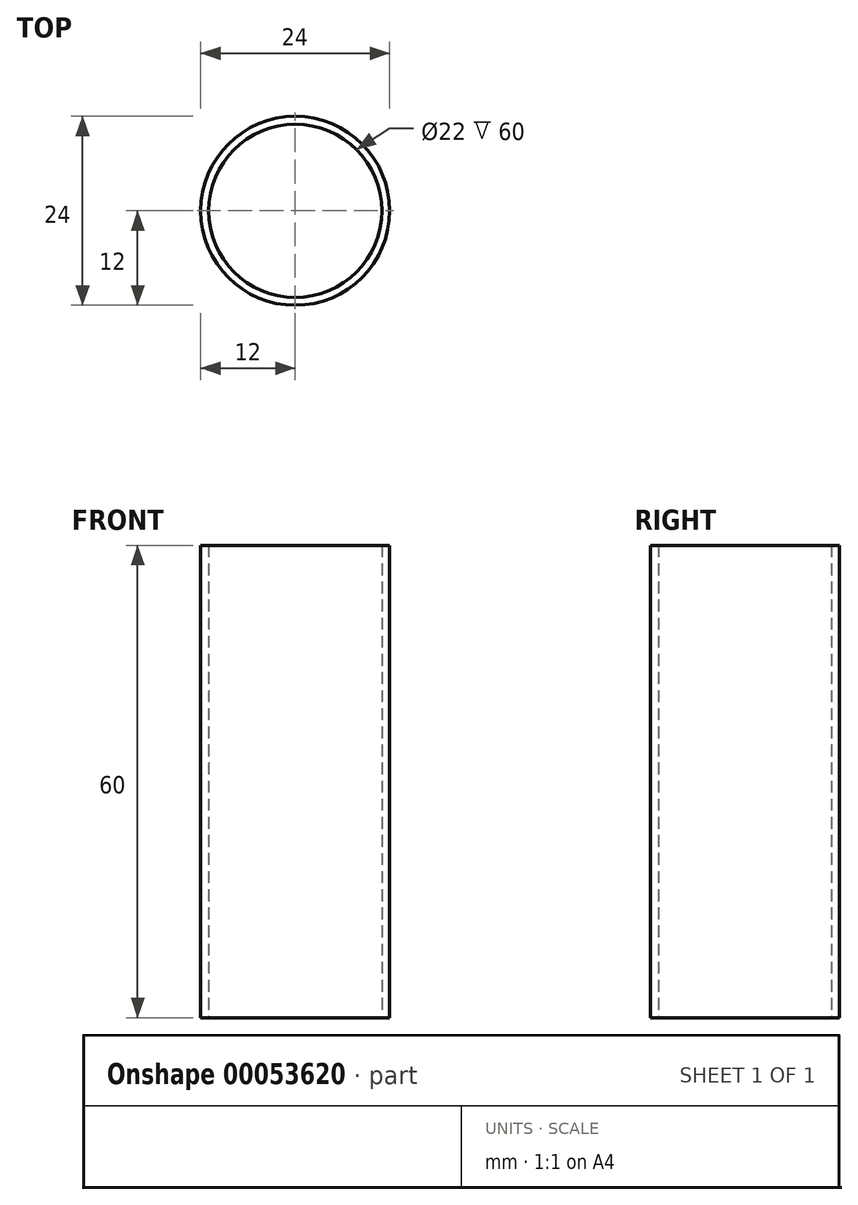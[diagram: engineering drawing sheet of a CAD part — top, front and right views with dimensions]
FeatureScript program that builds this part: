
annotation { "Feature Type Name" : "Feature", "Feature Type Description" : "" }
export const myFeature = defineFeature(function(context is Context, id is Id, definition is map)
    precondition{}
    {
        {
            var Q0;
            Q0=qCreatedBy(makeId("Top.planeOp"),FACE);
            var sketch = newSketch(context, id + "F0", { "sketchPlane" : qUnion([Q0])});
            skCircle(sketch, "E0", {"center": v(0, 0) * mm, "radius": 11 * mm});
            skCircle(sketch, "E1", {"center": v(0, 0) * mm, "radius": 12 * mm});
            skSolve(sketch);
        }
        {
            var Q0;
            Q0=makeQuery(id+"F0.imprint","IMPRINT",FACE,{"disambiguationData":[TD([[makeQuery(id+"F0.imprint","IMPRINT",EDGE,{"derivedFrom":sQuery(id+"F0.wireOp",EDGE,"E0")}),-1.0]])]});
            extrude(context, id + "F1", {"entities" : qUnion([Q0]), "depth" : 60 * mm});
        }
    });
